# Revit family: Haworth_Bac_Chair_One
name_source: partatom
category: Furniture
revit_build: Autodesk Revit 2018 (Build: 20170223_1515(x64)
units: mm (PartAtom-declared; Revit-internal decimal feet)

## family parameters
Always vertical = Yes
Cut with Voids When Loaded = No
OmniClass Number = 23.40.20.00
OmniClass Title = General Furniture and Specialties
Room Calculation Point = No
Shared = No
Work Plane-Based = No

## types (2) — shared parameters
Actual Depth = 1' - 7"
Actual Height = 2' - 5 1/2"
Actual Width = 1' - 5 3/4"
Assembly Code = E2020200
Depth = 19 in.
Height = 29.5 in.
Manufacturer = Haworth
Model = HCCE-BAC1
Revision = 1
Size = Verify Final Dim. w/ Haworth
URL = http://www.haworth.com
URL - Product = http://www.haworth.com
Warranty = http://www.haworth.com
Width = 17.75 in.

## per-type parameters (varying)
| type | Description | Upholstered Back | Wood Back |
| HCCE-BAC1 - Wood Back | Haworth Bac One Wood Back | No | Yes |
| HCCE-BAC1 - Upholstered Back | Haworth Bac One Upholstered Back | Yes | No |

## geometry (parser evidence)
native form markers: Sweep x3
no freeform markers — native parametric forms only
